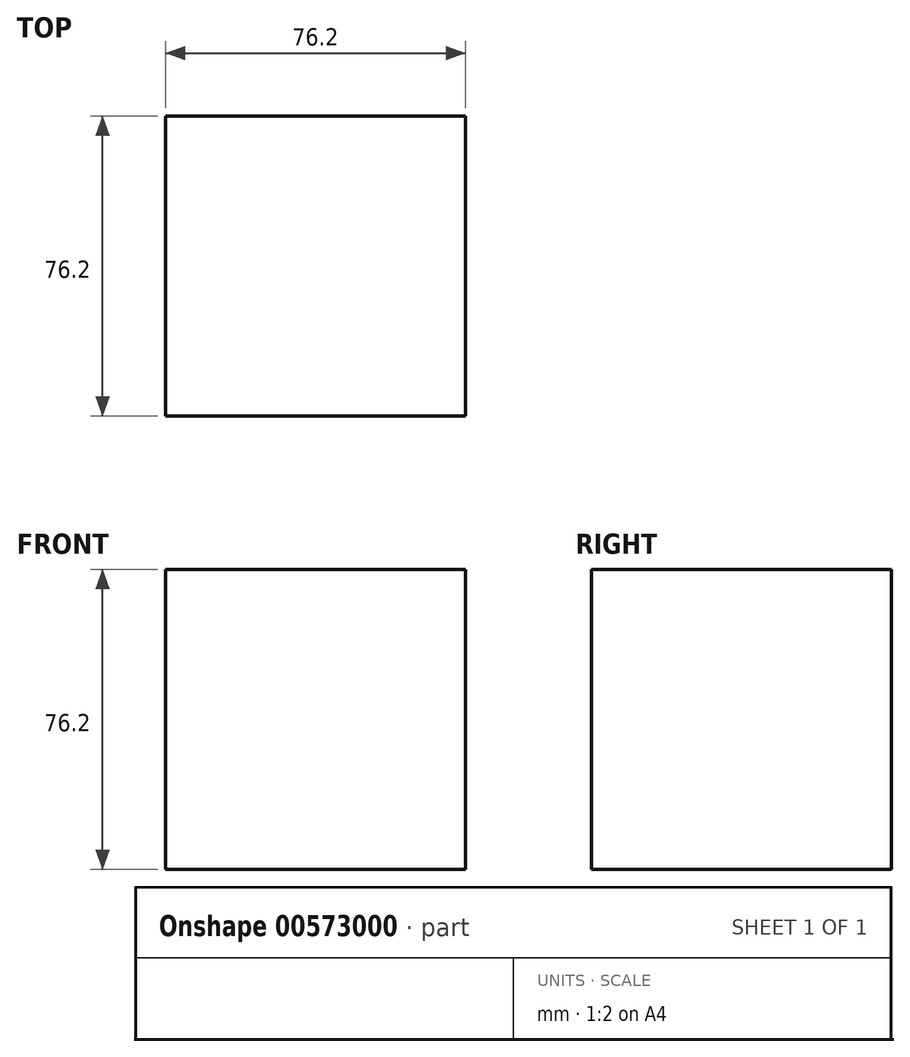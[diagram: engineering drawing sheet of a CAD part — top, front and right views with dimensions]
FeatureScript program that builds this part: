
annotation { "Feature Type Name" : "Feature", "Feature Type Description" : "" }
export const myFeature = defineFeature(function(context is Context, id is Id, definition is map)
    precondition{}
    {
        {
            var Q0;
            Q0=qCreatedBy(makeId("Front.planeOp"),FACE);
            var sketch = newSketch(context, id + "F0", { "sketchPlane" : qUnion([Q0])});
            skLineSegment(sketch, "E0.bottom", {"start": v(-26.74, 25.36) * mm, "end": v(49.46, 25.36) * mm});
            skLineSegment(sketch, "E0.top", {"start": v(-26.74, -50.84) * mm, "end": v(49.46, -50.84) * mm});
            skLineSegment(sketch, "E0.left", {"start": v(-26.74, 25.36) * mm, "end": v(-26.74, -50.84) * mm});
            skLineSegment(sketch, "E0.right", {"start": v(49.46, 25.36) * mm, "end": v(49.46, -50.84) * mm});
            skSolve(sketch);
        }
        {
            var Q0;
            Q0=makeQuery(id+"F0.imprint","IMPRINT",FACE,{"disambiguationData":[TD([[makeQuery(id+"F0.imprint","IMPRINT",EDGE,{"derivedFrom":sQuery(id+"F0.wireOp",EDGE,"E0.bottom")}),-1.0]])]});
            extrude(context, id + "F1", {"entities" : qUnion([Q0]), "depth" : 76.2 * mm, "offsetDistance" : 25.4 * mm});
        }
    });
